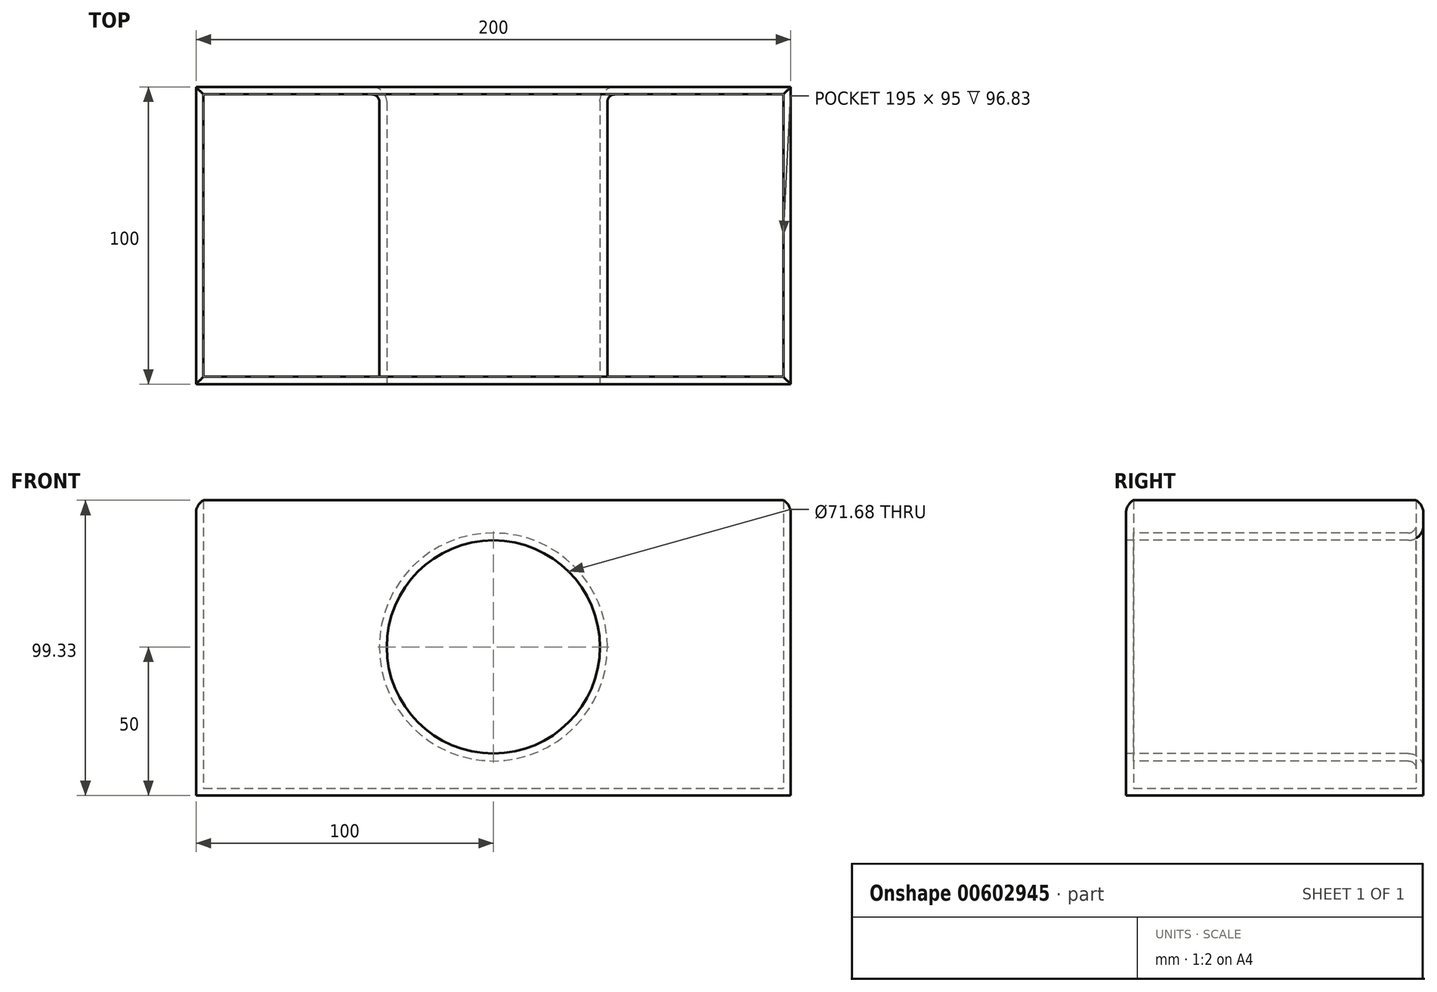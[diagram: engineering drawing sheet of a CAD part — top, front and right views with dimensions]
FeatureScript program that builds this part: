
annotation { "Feature Type Name" : "Feature", "Feature Type Description" : "" }
export const myFeature = defineFeature(function(context is Context, id is Id, definition is map)
    precondition{}
    {
        {
            var Q0;
            Q0=qCreatedBy(makeId("Front.planeOp"),FACE);
            var sketch = newSketch(context, id + "F0", { "sketchPlane" : qUnion([Q0])});
            skLineSegment(sketch, "E0.bottom", {"start": v(-100, 50) * mm, "end": v(100, 50) * mm});
            skLineSegment(sketch, "E0.top", {"start": v(-100, -50) * mm, "end": v(100, -50) * mm});
            skLineSegment(sketch, "E0.left", {"start": v(-100, 50) * mm, "end": v(-100, -50) * mm});
            skLineSegment(sketch, "E0.right", {"start": v(100, 50) * mm, "end": v(100, -50) * mm});
            skPoint(sketch, "E0.middle", {"position": v(0, 0) * mm});
            skSolve(sketch);
        }
        {
            var Q0;
            Q0=makeQuery(id+"F0.imprint","IMPRINT",FACE,{"disambiguationData":[TD([[makeQuery(id+"F0.imprint","IMPRINT",EDGE,{"derivedFrom":sQuery(id+"F0.wireOp",EDGE,"E0.bottom")}),-1.0]])]});
            extrude(context, id + "F1", {"entities" : qUnion([Q0]), "depth" : 100 * mm, "offsetDistance" : 25 * mm});
        }
        {
            var Q0;
            Q0=makeQuery(id+"F1.opExtrude","CAP_FACE",FACE,{"disambiguationData":[OSD([sQuery(id+"F0.wireOp",EDGE,"E0.bottom"),sQuery(id+"F0.wireOp",EDGE,"E0.top"),sQuery(id+"F0.wireOp",EDGE,"E0.left"),sQuery(id+"F0.wireOp",EDGE,"E0.right")])],"isStart":false});
            var sketch = newSketch(context, id + "F2", { "sketchPlane" : qUnion([Q0])});
            skCircle(sketch, "E1", {"center": v(0, 0) * mm, "radius": 35.84 * mm});
            skSolve(sketch);
        }
        {
            var Q0;
            Q0=makeQuery(id+"F2.imprint","IMPRINT",FACE,{"disambiguationData":[TD([[makeQuery(id+"F2.imprint","IMPRINT",EDGE,{"derivedFrom":sQuery(id+"F2.wireOp",EDGE,"E1")}),1.0]])]});
            extrude(context, id + "F3", {"entities" : qUnion([Q0]), "operationType" : NewBodyOperationType.REMOVE, "endBound" : BoundingType.THROUGH_ALL, "oppositeDirection" : true, "depth" : 25 * mm, "offsetDistance" : 25 * mm});
        }
        {
            var Q0;
            Q0=makeQuery(id+"F3.boolean.opBoolean","COPY",EDGE,{"derivedFrom":makeQuery(id+"F3.opExtrude","CAP_EDGE",EDGE,{"disambiguationData":[OSD([sQuery(id+"F2.wireOp",EDGE,"E1")])],"isStart":true})});
            var Q1;
            Q1=makeQuery(id+"F3.boolean.opBoolean","INTERSECT",EDGE,{"derivedFrom":[makeQuery(id+"F1.opExtrude","CAP_FACE",FACE,{"disambiguationData":[OSD([sQuery(id+"F0.wireOp",EDGE,"E0.bottom"),sQuery(id+"F0.wireOp",EDGE,"E0.top"),sQuery(id+"F0.wireOp",EDGE,"E0.left"),sQuery(id+"F0.wireOp",EDGE,"E0.right")])],"isStart":true}),makeQuery(id+"F3.opExtrude","SWEPT_FACE",FACE,{"disambiguationData":[OSD([sQuery(id+"F2.wireOp",EDGE,"E1")])]})]});
            fillet(context, id + "F4", {"entities" : qUnion([Q0, Q1]), "radius" : 5 * mm, "tangentPropagation" : true, "allowEdgeOverflow" : false});
        }
        {
            var Q0;
            Q0=makeQuery(id+"F1.opExtrude","SWEPT_FACE",FACE,{"disambiguationData":[OSD([sQuery(id+"F0.wireOp",EDGE,"E0.bottom")])]});
            shell(context, id + "F5", {"entities" : qUnion([Q0]), "thickness" : 2.5 * mm});
        }
        {
            var Q0;
            Q0=makeQuery(id+"F1.opExtrude","CAP_EDGE",EDGE,{"disambiguationData":[OSD([sQuery(id+"F0.wireOp",EDGE,"E0.bottom")])],"isStart":false});
            var Q1;
            Q1=makeQuery(id+"F1.opExtrude","SWEPT_EDGE",EDGE,{"disambiguationData":[OSD([sQuery(id+"F0.wireOp",EDGE,"E0.bottom"),sQuery(id+"F0.wireOp",EDGE,"E0.left")])]});
            var Q2;
            Q2=makeQuery(id+"F1.opExtrude","CAP_EDGE",EDGE,{"disambiguationData":[OSD([sQuery(id+"F0.wireOp",EDGE,"E0.bottom")])],"isStart":true});
            var Q3;
            Q3=makeQuery(id+"F1.opExtrude","SWEPT_EDGE",EDGE,{"disambiguationData":[OSD([sQuery(id+"F0.wireOp",EDGE,"E0.bottom"),sQuery(id+"F0.wireOp",EDGE,"E0.right")])]});
            fillet(context, id + "F6", {"entities" : qUnion([Q0, Q1, Q2, Q3]), "radius" : 5 * mm, "tangentPropagation" : true, "allowEdgeOverflow" : false});
        }
    });
